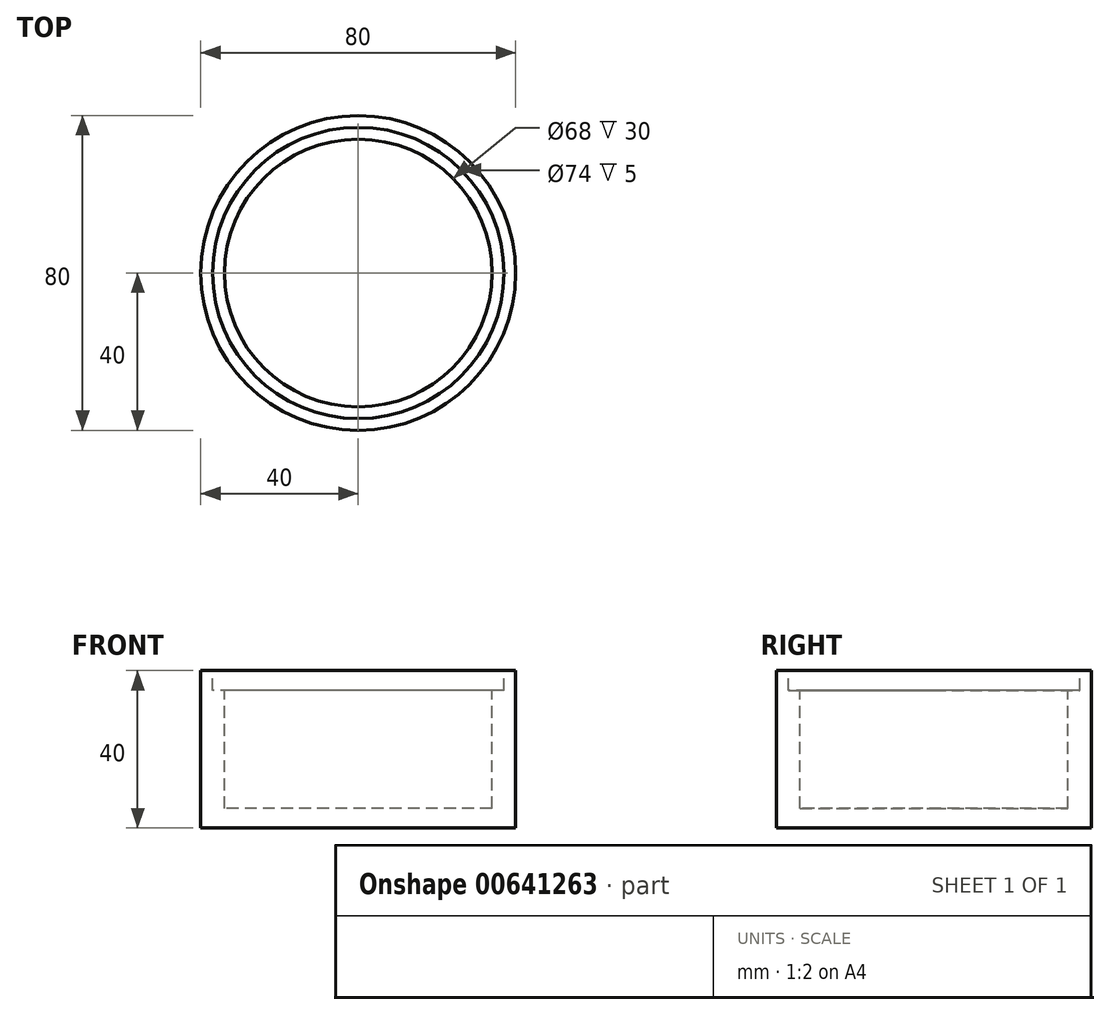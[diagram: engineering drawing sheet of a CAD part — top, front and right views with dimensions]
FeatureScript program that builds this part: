
annotation { "Feature Type Name" : "Feature", "Feature Type Description" : "" }
export const myFeature = defineFeature(function(context is Context, id is Id, definition is map)
    precondition{}
    {
        {
            var Q0;
            Q0=qCreatedBy(makeId("Front.planeOp"),FACE);
            var sketch = newSketch(context, id + "F0", { "sketchPlane" : qUnion([Q0])});
            skLineSegment(sketch, "E0", {"start": v(0, 0) * mm, "end": v(-40, 0) * mm});
            skLineSegment(sketch, "E1", {"start": v(-40, 0) * mm, "end": v(-40, 40) * mm});
            skLineSegment(sketch, "E2", {"start": v(-40, 40) * mm, "end": v(-37, 40) * mm});
            skLineSegment(sketch, "E3", {"start": v(-37, 40) * mm, "end": v(-37, 35) * mm});
            skLineSegment(sketch, "E4", {"start": v(-37, 35) * mm, "end": v(-34, 35) * mm});
            skLineSegment(sketch, "E5", {"start": v(-34, 35) * mm, "end": v(-34, 5) * mm});
            skLineSegment(sketch, "E6", {"start": v(-34, 5) * mm, "end": v(0, 5) * mm});
            skLineSegment(sketch, "E7", {"start": v(0, 5) * mm, "end": v(0, 0) * mm});
            skSolve(sketch);
        }
        {
            var Q0;
            Q0=makeQuery(id+"F0.imprint","IMPRINT",FACE,{"disambiguationData":[TD([[makeQuery(id+"F0.imprint","IMPRINT",EDGE,{"derivedFrom":sQuery(id+"F0.wireOp",EDGE,"E0")}),-1.0]])]});
            var Q1;
            Q1=sQuery(id+"F0.wireOp",EDGE,"E7");
            revolve(context, id + "F1", {"entities" : qUnion([Q0]), "axis" : qUnion([Q1]), "revolveType" : RevolveType.FULL});
        }
    });
